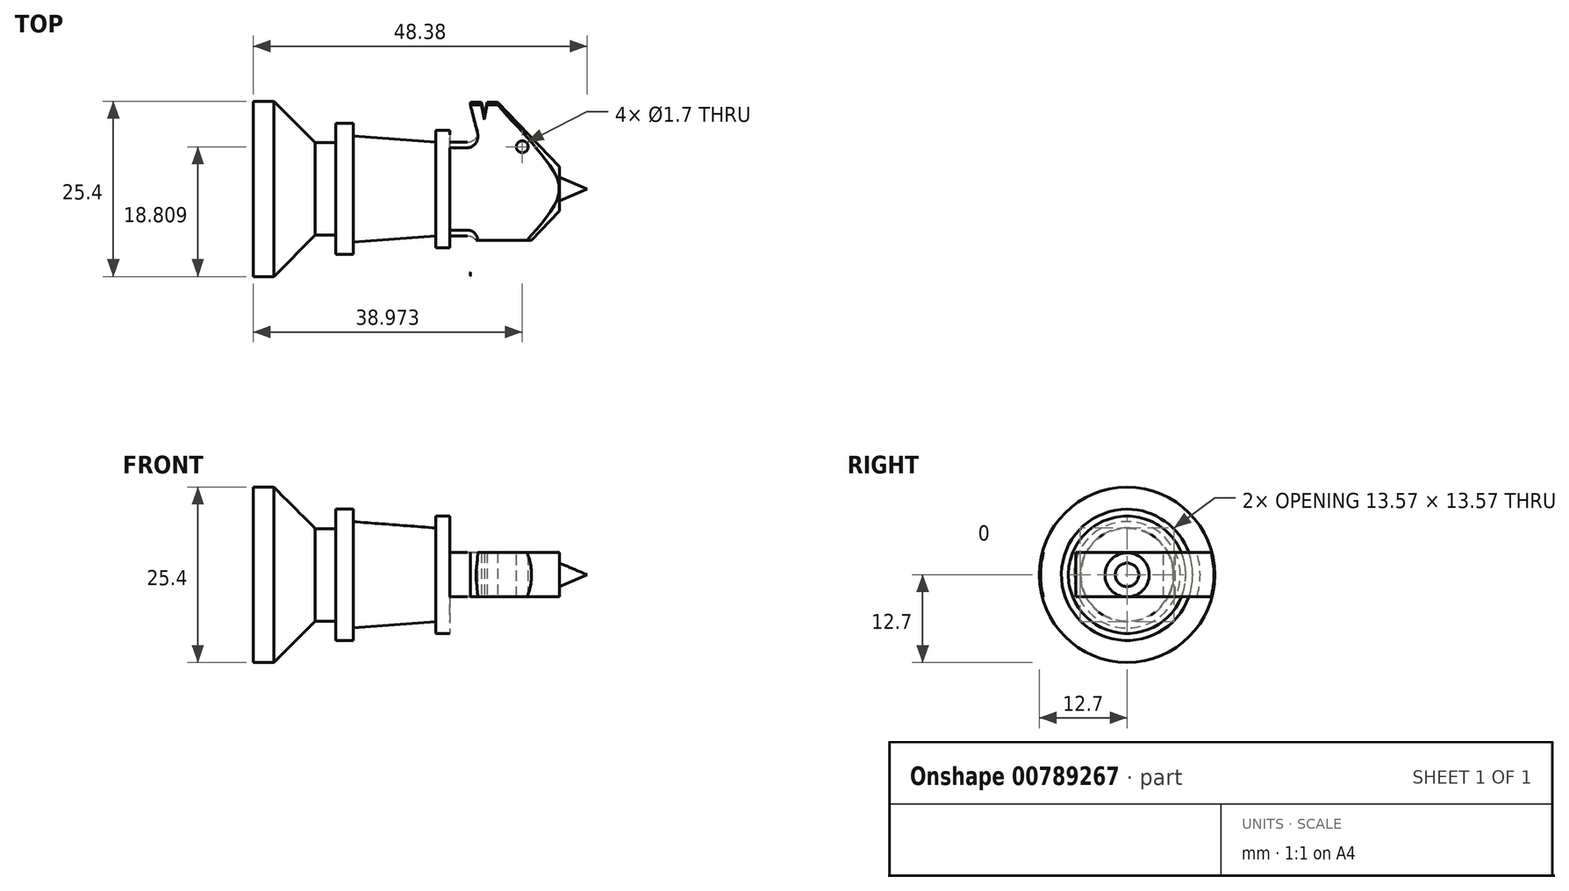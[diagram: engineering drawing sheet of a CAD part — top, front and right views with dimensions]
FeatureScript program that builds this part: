
annotation { "Feature Type Name" : "Feature", "Feature Type Description" : "" }
export const myFeature = defineFeature(function(context is Context, id is Id, definition is map)
    precondition{}
    {
        {
            var Q0;
            Q0=qCreatedBy(makeId("Front.planeOp"),FACE);
            var sketch = newSketch(context, id + "F0", { "sketchPlane" : qUnion([Q0])});
            skLineSegment(sketch, "E0", {"start": v(0, 0) * mm, "end": v(-4, 1.7) * mm});
            skLineSegment(sketch, "E1", {"start": v(-4, 1.7) * mm, "end": v(-4, 3.2) * mm});
            skLineSegment(sketch, "E2", {"start": v(-4, 3.2) * mm, "end": v(-13, 12.58) * mm});
            skLineSegment(sketch, "E3", {"start": v(-13, 12.58) * mm, "end": v(-14.5, 12.58) * mm});
            skLineSegment(sketch, "E4", {"start": v(-15.32, 12.58) * mm, "end": v(-16.92, 12.58) * mm});
            skLineSegment(sketch, "E5", {"start": v(-19.92, 6.79) * mm, "end": v(-19.92, 8.5) * mm});
            skLineSegment(sketch, "E6", {"start": v(-19.92, 8.5) * mm, "end": v(-21.92, 8.5) * mm});
            skLineSegment(sketch, "E7", {"start": v(-21.92, 8.5) * mm, "end": v(-21.92, 6.79) * mm});
            skLineSegment(sketch, "E8", {"start": v(-21.92, 6.79) * mm, "end": v(-33.89, 7.7) * mm});
            skLineSegment(sketch, "E9", {"start": v(-33.88, 9.5) * mm, "end": v(-36.38, 9.5) * mm});
            skLineSegment(sketch, "E10", {"start": v(-36.38, 9.5) * mm, "end": v(-36.38, 6.7) * mm});
            skLineSegment(sketch, "E11", {"start": v(-33.88, 9.5) * mm, "end": v(-33.89, 7.7) * mm});
            skLineSegment(sketch, "E12", {"start": v(-36.38, 6.7) * mm, "end": v(-39.38, 6.7) * mm});
            skLineSegment(sketch, "E13", {"start": v(-39.38, 6.7) * mm, "end": v(-45.38, 12.7) * mm});
            skLineSegment(sketch, "E14", {"start": v(-45.38, 12.7) * mm, "end": v(-48.38, 12.7) * mm});
            skLineSegment(sketch, "E15", {"start": v(-48.38, 12.7) * mm, "end": v(-48.38, 0) * mm});
            skLineSegment(sketch, "E16", {"start": v(-48.38, 0) * mm, "end": v(0, 0) * mm});
            skLineSegment(sketch, "E17", {"start": v(-14.9, 10.58) * mm, "end": v(-15.32, 12.58) * mm});
            skLineSegment(sketch, "E18", {"start": v(-14.9, 10.58) * mm, "end": v(-14.5, 12.58) * mm});
            skLineSegment(sketch, "E19", {"start": v(-16.92, 12.58) * mm, "end": v(-15.88, 8.68) * mm});
            skLineSegment(sketch, "E20", {"start": v(-17.33, 6.79) * mm, "end": v(-19.92, 6.79) * mm});
            skPoint(sketch, "E21.visualSharp", {"position": v(-15.37, 6.79) * mm});
            skArc(sketch, "E21.filletArc", {"start": v(-17.33, 6.79) * mm, "mid": v(-16.14, 7.37) * mm, "end": v(-15.88, 8.68) * mm});
            skSolve(sketch);
        }
        {
            var Q0;
            Q0 = qSketchRegion(id + "F0", true);
            var Q1;
            Q1=sQuery(id+"F0.wireOp",EDGE,"E16");
            revolve(context, id + "F1", {"surfaceOperationType" : NewSurfaceOperationType.NEW, "entities" : qUnion([Q0]), "axis" : qUnion([Q1]), "revolveType" : RevolveType.FULL});
        }
        {
            var Q0;
            Q0=qCreatedBy(makeId("Front.planeOp"),FACE);
            cPlane(context, id + "F2", {"entities" : qUnion([Q0]), "cplaneType" : CPlaneType.OFFSET, "offset" : 12.7 * mm, "width" : 150 * mm, "height" : 150 * mm});
        }
        {
            var Q0;
            Q0=qCreatedBy(id+"F2.planeOp",FACE);
            var sketch = newSketch(context, id + "F3", { "sketchPlane" : qUnion([Q0])});
            skLineSegment(sketch, "E22", {"start": v(-3.92, 3.22) * mm, "end": v(-19.92, 3.22) * mm});
            skLineSegment(sketch, "E23", {"start": v(-19.92, 3.22) * mm, "end": v(-19.92, 15.92) * mm});
            skLineSegment(sketch, "E24", {"start": v(-19.92, 15.92) * mm, "end": v(-3.92, 15.92) * mm});
            skLineSegment(sketch, "E25", {"start": v(-3.92, 15.92) * mm, "end": v(-3.92, 3.22) * mm});
            skLineSegment(sketch, "E26", {"start": v(-3.88, -3.2) * mm, "end": v(-19.92, -3.2) * mm});
            skLineSegment(sketch, "E27", {"start": v(-19.92, -3.2) * mm, "end": v(-19.92, -15.7) * mm});
            skLineSegment(sketch, "E28", {"start": v(-19.92, -15.7) * mm, "end": v(-3.88, -15.7) * mm});
            skLineSegment(sketch, "E29", {"start": v(-3.88, -15.7) * mm, "end": v(-3.88, -3.2) * mm});
            skSolve(sketch);
        }
        {
            var Q0;
            Q0=makeQuery(id+"F3.imprint","IMPRINT",FACE,{"disambiguationData":[TD([[makeQuery(id+"F3.imprint","IMPRINT",EDGE,{"derivedFrom":sQuery(id+"F3.wireOp",EDGE,"E22")}),-1.0]])]});
            var Q1;
            Q1=makeQuery(id+"F3.imprint","IMPRINT",FACE,{"disambiguationData":[TD([[makeQuery(id+"F3.imprint","IMPRINT",EDGE,{"derivedFrom":sQuery(id+"F3.wireOp",EDGE,"E26")}),1.0]])]});
            extrude(context, id + "F4", {"entities" : qUnion([Q0, Q1]), "operationType" : NewBodyOperationType.REMOVE, "oppositeDirection" : true, "depth" : 45 * mm, "offsetDistance" : 25 * mm});
        }
        {
            var Q0;
            Q0=makeQuery(id+"F4.boolean.opBoolean","COPY",FACE,{"derivedFrom":makeQuery(id+"F4.opExtrude","SWEPT_FACE",FACE,{"disambiguationData":[OSD([sQuery(id+"F3.wireOp",EDGE,"E22")])]})});
            var sketch = newSketch(context, id + "F5", { "sketchPlane" : qUnion([Q0])});
            skLineSegment(sketch, "E30", {"start": v(-16.9, -7.44) * mm, "end": v(-7.9, -7.44) * mm});
            skLineSegment(sketch, "E31", {"start": v(-7.9, -7.44) * mm, "end": v(-7.9, -15.44) * mm});
            skLineSegment(sketch, "E32", {"start": v(-7.9, -15.44) * mm, "end": v(-16.9, -15.44) * mm});
            skLineSegment(sketch, "E33", {"start": v(-16.9, -15.44) * mm, "end": v(-16.9, -7.44) * mm});
            skSolve(sketch);
        }
        {
            var Q0;
            Q0 = qSketchRegion(id + "F5", true);
            extrude(context, id + "F6", {"entities" : qUnion([Q0]), "operationType" : NewBodyOperationType.REMOVE, "oppositeDirection" : true, "depth" : 25 * mm, "offsetDistance" : 25 * mm});
        }
        {
            var Q0;
            Q0=makeQuery(id+"F4.boolean.opBoolean","COPY",FACE,{"derivedFrom":makeQuery(id+"F4.opExtrude","SWEPT_FACE",FACE,{"disambiguationData":[OSD([sQuery(id+"F3.wireOp",EDGE,"E22")])]})});
            var sketch = newSketch(context, id + "F7", { "sketchPlane" : qUnion([Q0])});
            skCircle(sketch, "E34", {"center": v(-9.4, 6.1) * mm, "radius": 0.85 * mm});
            skSolve(sketch);
        }
        {
            var Q0;
            Q0=makeQuery(id+"F7.imprint","IMPRINT",FACE,{"disambiguationData":[TD([[makeQuery(id+"F7.imprint","IMPRINT",EDGE,{"derivedFrom":sQuery(id+"F7.wireOp",EDGE,"E34")}),1.0]])]});
            extrude(context, id + "F8", {"entities" : qUnion([Q0]), "operationType" : NewBodyOperationType.REMOVE, "oppositeDirection" : true, "depth" : 50 * mm, "offsetDistance" : 25 * mm});
        }
    });
